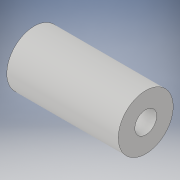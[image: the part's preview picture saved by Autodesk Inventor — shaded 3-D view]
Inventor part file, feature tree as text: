
AUTODESK INVENTOR PART (.ipt)
format: ipt  version: 2017 SP1 (Build 210196100, 196)  size: 94,720 bytes
history: native  units: in
note: dims shown in document units (in); Inventor stores cm internally (conversion verified against a paired STEP export)
features: extrude x1, sketch x1
ambient origin geometry x8: Origin, YZ Plane, XZ Plane, XY Plane, X Axis, Y Axis, Z Axis, Center Point
bodies: Solid1 (feature_tree)
feature tree (2):
  extrude  "Extrusion1"  Depth=14.0in
  sketch  "Sketch1"  dims[d0=6.9in d1=2.75in d2=14.0in d3=0.0in]
